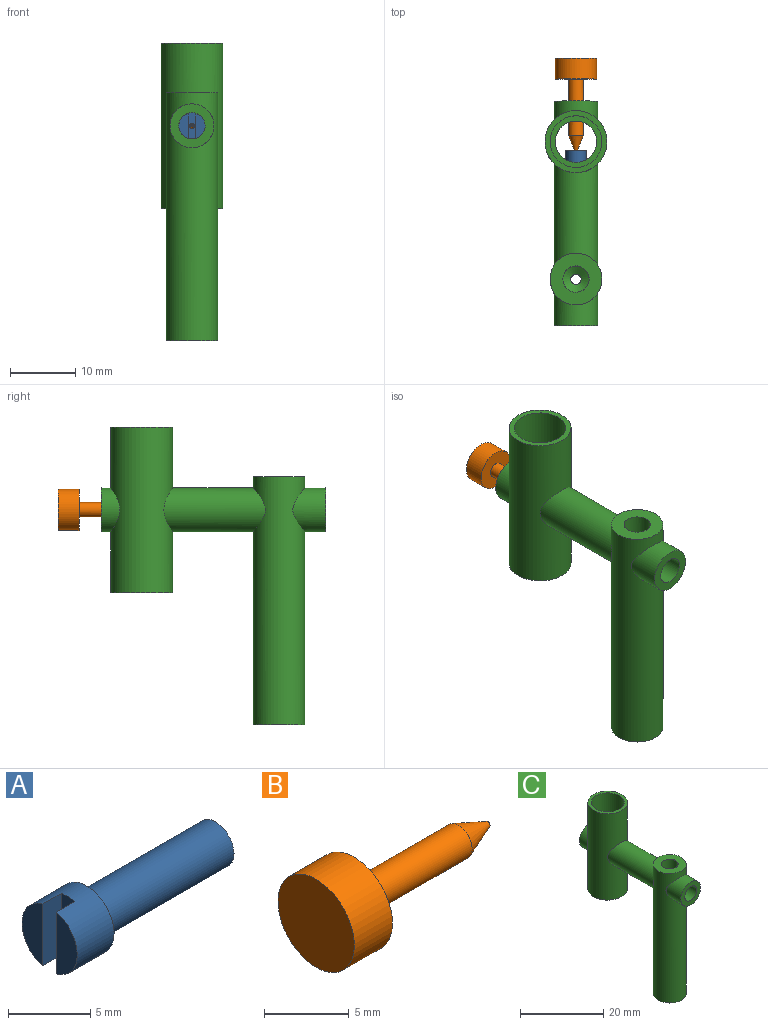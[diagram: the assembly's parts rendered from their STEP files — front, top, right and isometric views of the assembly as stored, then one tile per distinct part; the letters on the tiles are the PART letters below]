
ASSEMBLY  parts=3 mates=2
PART A: 10 faces, bbox 14.3x4.8x4.8 mm
  f0: plane 4.6x1.78mm, normal (-1,0,0), area 6.1mm2, adj f2,f7
  f1: cylinder r=0.4mm len=12.7mm, axis (1,0,0), area 31.7mm2, adj f6,f9
  f2: cylinder r=2.37mm len=4.75mm, axis (-1,0,0), area 43.6mm2, adj f0,f3,f4,f7,f8,f9
  f3: plane 4.75x4.75mm, normal (1,0,0), area 9.8mm2, adj f2,f5
  f4: plane 4.6x1.78mm, normal (-1,0,0), area 6.1mm2, adj f2,f8
  f5: cylinder r=1.59mm len=11.11mm, axis (-1,0,0), area 110.8mm2, adj f3,f6
  f6: plane 3.18x3.18mm, normal (1,0,0), area 7.4mm2, adj f1,f5
  f7: plane 4.6x1.59mm, normal (0,-1,0), area 7.3mm2, adj f0,f2,f9
  f8: plane 4.6x1.59mm, normal (0,1,0), area 7.3mm2, adj f2,f4,f9
  f9: plane 4.75x1.19mm, normal (-1,0,0), area 5.1mm2, adj f1,f2,f7,f8
PART B: 6 faces, bbox 14.3x6.4x6.4 mm
  f0: cylinder r=3.17mm len=6.35mm, axis (-1,0,0), area 63.3mm2, adj f1,f2
  f1: plane 6.35x6.35mm, normal (1,0,0), area 27.7mm2, adj f0,f3
  f2: plane 6.35x6.35mm, normal (-1,0,0), area 31.7mm2, adj f0
  f3: cylinder r=1.13mm len=8.67mm, axis (-1,0,0), area 61.6mm2, adj f1,f4
  f4: cone r=0.11mm half-angle=21.4deg, axis (-1,0,0), area 10.7mm2, adj f3,f5
  f5: plane 0.35x0.35mm, normal (1,0,0), area 0.1mm2, adj f4
PART C: 25 faces, bbox 9.5x34.5x45.7 mm
  f0: cylinder r=3.17mm len=15.88mm, axis (0,0,1), area 304.8mm2, adj f11,f15,f21,f22,f23,f24
  f1: cylinder r=0.79mm len=27.84mm, axis (0,0,-1), area 138.8mm2, adj f6,f17
  f2: cylinder r=2.02mm len=7.14mm, axis (0,-1,0), area 74.3mm2, adj f7,f16,f18
  f3: cylinder r=3.37mm len=15.62mm, axis (0,-1,0), area 293.7mm2, adj f4,f9
  f4: cylinder r=3.97mm len=38.1mm, axis (0,0,-1), area 869.6mm2, adj f3,f5,f6,f8
  f5: plane 7.94x7.94mm, normal (0,0,1), area 36.7mm2, adj f4,f18
  f6: plane 7.94x7.94mm, normal (0,0,-1), area 47.5mm2, adj f1,f4
  f7: plane 6.73x6.73mm, normal (0,-1,0), area 22.8mm2, adj f2,f8
  f8: cylinder r=3.37mm len=6.73mm, axis (0,-1,0), area 85.4mm2, adj f4,f7
  f9: cylinder r=4.76mm len=25.4mm, axis (0,0,-1), area 683.3mm2, adj f3,f10,f11,f13
  f10: plane 9.53x9.53mm, normal (0,0,1), area 21.8mm2, adj f9,f14
  f11: plane 9.53x9.53mm, normal (0,0,-1), area 39.6mm2, adj f0,f9
  f12: plane 6.73x6.73mm, normal (0,1,0), area 31.6mm2, adj f13,f24
  f13: cylinder r=3.37mm len=6.73mm, axis (0,-1,0), area 45.6mm2, adj f9,f12
  f14: cylinder r=3.97mm len=9.53mm, axis (0,0,1), area 237.5mm2, adj f10,f15
  f15: plane 7.94x7.94mm, normal (0,0,1), area 17.8mm2, adj f0,f14
  f16: cylinder r=2.02mm len=4.45mm, axis (0,0,1), area 40.1mm2, adj f2,f17,f20
  f17: cone r=0mm half-angle=59deg, axis (0,0,1), area 12.6mm2, adj f1,f16
  f18: cylinder r=2.02mm len=5.08mm, axis (0,0,1), area 48.1mm2, adj f2,f5,f20
  f19: plane 4.04x4.04mm, normal (0,-1,0), area 4.9mm2, adj f20,f23
  f20: cylinder r=2.02mm len=8.73mm, axis (0,-1,0), area 94.5mm2, adj f16,f18,f19
  f21: plane 1.41x0.17mm, normal (0,-1,0), area 0.2mm2, adj f0,f23
  f22: plane 1.41x0.17mm, normal (0,-1,0), area 0.2mm2, adj f0,f23
  f23: cylinder r=1.59mm len=9.53mm, axis (0,-1,0), area 93.6mm2, adj f0,f19,f21,f22
  f24: cylinder r=1.13mm len=3.29mm, axis (0,1,0), area 22.6mm2, adj f0,f12
PLACE A rot(axis=(0,0,1),90deg) t=(-9.73,34.82,31.4)mm
PLACE B rot(axis=(0,0,-1),90deg) t=(-9.73,63.27,31.4)mm
PLACE C t=(-9.73,29.37,-1.62)mm fixed
MATE slider B.f3 <-> C.f2  axis (0,1,0) through (-9.73,55.76,31.4)mm
MATE slider A.f5 <-> C.f2  axis (0,-1,0) through (-9.73,43.55,31.4)mm
